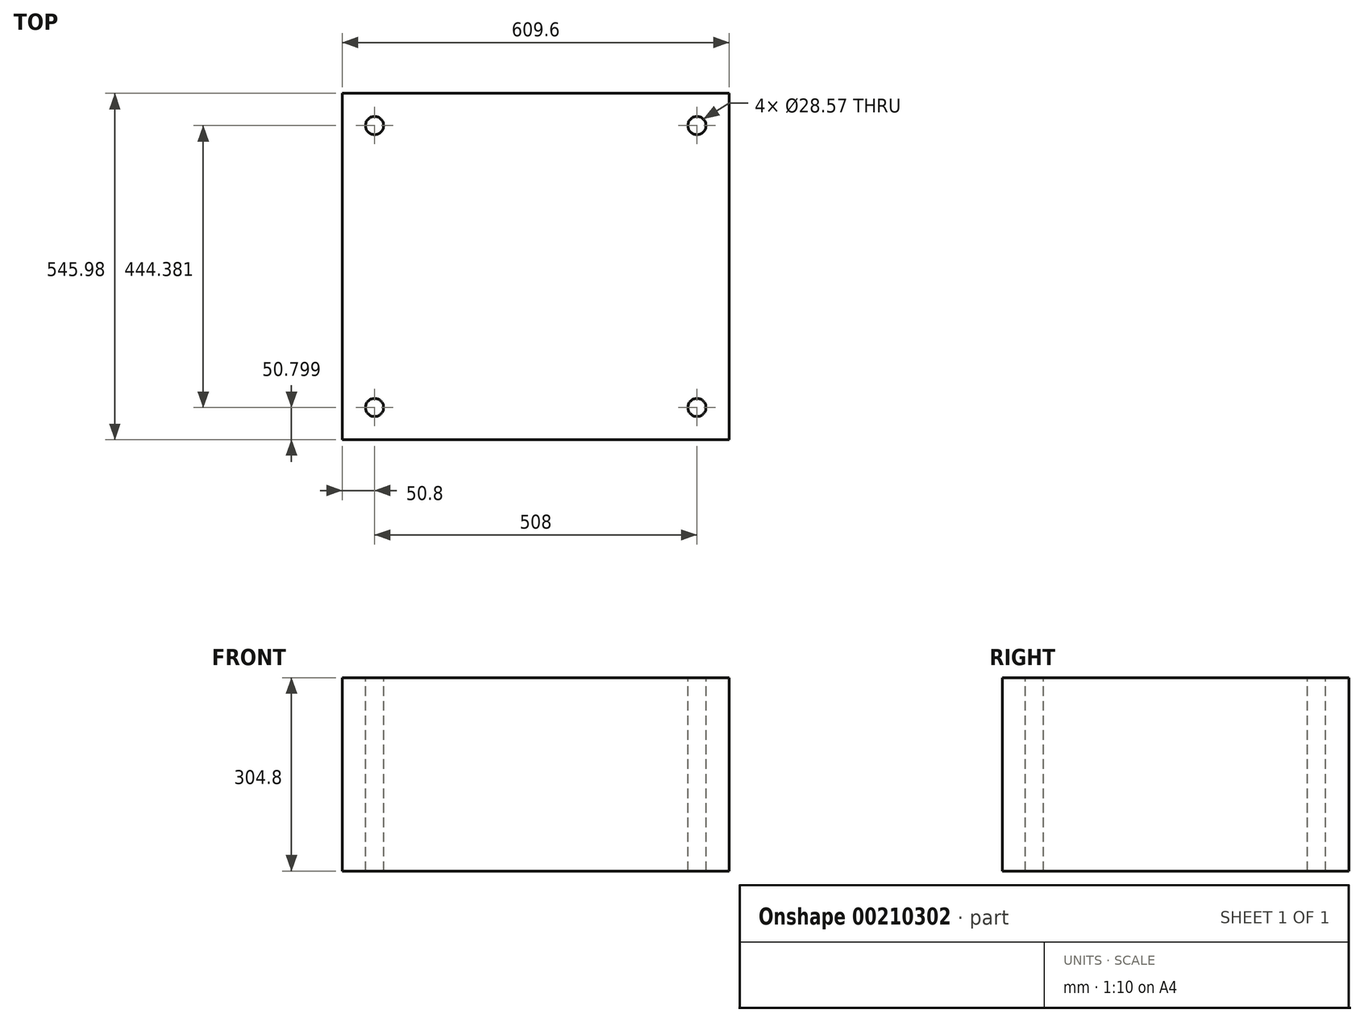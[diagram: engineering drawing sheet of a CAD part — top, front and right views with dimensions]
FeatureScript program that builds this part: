
annotation { "Feature Type Name" : "Feature", "Feature Type Description" : "" }
export const myFeature = defineFeature(function(context is Context, id is Id, definition is map)
    precondition{}
    {
        {
            var Q0;
            Q0=qCreatedBy(makeId("Top.planeOp"),FACE);
            var sketch = newSketch(context, id + "F0", { "sketchPlane" : qUnion([Q0])});
            skLineSegment(sketch, "E0.bottom", {"start": v(304.8, 273) * mm, "end": v(-304.8, 273) * mm});
            skLineSegment(sketch, "E0.top", {"start": v(304.8, -273) * mm, "end": v(-304.8, -273) * mm});
            skLineSegment(sketch, "E0.left", {"start": v(304.8, 273) * mm, "end": v(304.8, -273) * mm});
            skLineSegment(sketch, "E0.right", {"start": v(-304.8, 273) * mm, "end": v(-304.8, -273) * mm});
            skPoint(sketch, "E0.middle", {"position": v(0, 0) * mm});
            skSolve(sketch);
        }
        {
            var Q0;
            Q0 = qSketchRegion(id + "F0", true);
            extrude(context, id + "F1", {"entities" : qUnion([Q0]), "depth" : 304.8 * mm});
        }
        {
            var Q0;
            Q0=makeQuery(id+"F1.opExtrude","CAP_FACE",FACE,{"disambiguationData":[OSD([sQuery(id+"F0.wireOp",EDGE,"E0.bottom"),sQuery(id+"F0.wireOp",EDGE,"E0.top"),sQuery(id+"F0.wireOp",EDGE,"E0.left"),sQuery(id+"F0.wireOp",EDGE,"E0.right")])],"isStart":false});
            var sketch = newSketch(context, id + "F2", { "sketchPlane" : qUnion([Q0])});
            skCircle(sketch, "E1", {"center": v(-254, -222.2) * mm, "radius": 14.29 * mm});
            skLineSegment(sketch, "E2", {"start": v(0, 142.04) * mm, "end": v(0, -353) * mm, "construction": true});
            skPoint(sketch, "E2.endSnap0", {"position": v(0, -273) * mm});
            skCircle(sketch, "E3.MirrorC", {"center": v(254, -222.2) * mm, "radius": 14.29 * mm});
            skLineSegment(sketch, "E4", {"start": v(-280.66, 0) * mm, "end": v(360.74, 0) * mm, "construction": true});
            skCircle(sketch, "E5.MirrorC", {"center": v(-254, 222.2) * mm, "radius": 14.29 * mm});
            skCircle(sketch, "E6.MirrorC", {"center": v(254, 222.2) * mm, "radius": 14.29 * mm});
            skSolve(sketch);
        }
        {
            var Q0;
            Q0=sQuery(id+"F2.wireOp",VERTEX,"E3.MirrorC.center");
            var Q1;
            Q1=sQuery(id+"F2.wireOp",VERTEX,"E6.MirrorC.center");
            var Q2;
            Q2=sQuery(id+"F2.wireOp",VERTEX,"E1.center");
            var Q3;
            Q3=sQuery(id+"F2.wireOp",VERTEX,"E5.MirrorC.center");
            var Q4;
            Q4=makeQuery(id+"F1.opExtrude","SWEPT_BODY",BODY,{"disambiguationData":[OSD([sQuery(id+"F0.wireOp",EDGE,"E0.bottom"),sQuery(id+"F0.wireOp",EDGE,"E0.top"),sQuery(id+"F0.wireOp",EDGE,"E0.left"),sQuery(id+"F0.wireOp",EDGE,"E0.right")])]});
            hole(context, id + "F3", {"style" : HoleStyle.SIMPLE, "endStyle" : HoleEndStyle.THROUGH, "holeDiameter" : 28.57 * mm, "locations" : qUnion([Q0, Q1, Q2, Q3]), "scope" : qUnion([Q4]), "isTappedThrough" : true});
        }
    });
